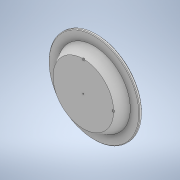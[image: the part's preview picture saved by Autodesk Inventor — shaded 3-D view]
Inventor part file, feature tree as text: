
AUTODESK INVENTOR PART (.ipt)
format: ipt  version: 2020 (Build 240168000, 168)  size: 173,056 bytes
history: native  units: in
note: dims shown in document units (in); Inventor stores cm internally (conversion verified against a paired STEP export)
features: sketch x3, extrude x2, chamfer x2, revolve x1, shell x1
ambient origin geometry x8: Origin, YZ Plane, XZ Plane, XY Plane, X Axis, Y Axis, Z Axis, Center Point
bodies: Solid1 (feature_tree)
feature tree (9):
  extrude  "Extrusion1"  Depth=0.1575in TaperAngle=0.0deg
  revolve  "Revolution2"  [1 undecoded]
  shell  "Shell1"  Thickness=90.0deg
  chamfer  "Chamfer2"  Distance=0.1969in
  chamfer  "Chamfer3"  Distance=0.3937in
  extrude  "Extrusion4"  Depth=0.0787in TaperAngle=45.0deg
  sketch  "Sketch1"  dims[d0=11.811in d1=0.1575in d2=0.0in]
  sketch  "Sketch5"  dims[d16=1.5748in d17=3.937in d18=90.0deg]
  sketch  "Sketch7"  dims[d21=1.1811in d22=0.1969in d26=0.3937in d27=0.0787in d28=0.0787in d29=45.0deg d30=0.0787in d31=0.0787in d32=45.0deg d33=0.2362in d34=0.7874in d35=3.7402in d36=0.7874in d38=90.0deg d40=0.0787in d41=0.0in d42=0.1575in d3=0.0197in d4=0.0344in]
note: 1 required parameter value undecoded (feature->parameter linkage not recoverable at this tier; creation-order binding heuristic only, values carry confidence <= 0.55)
